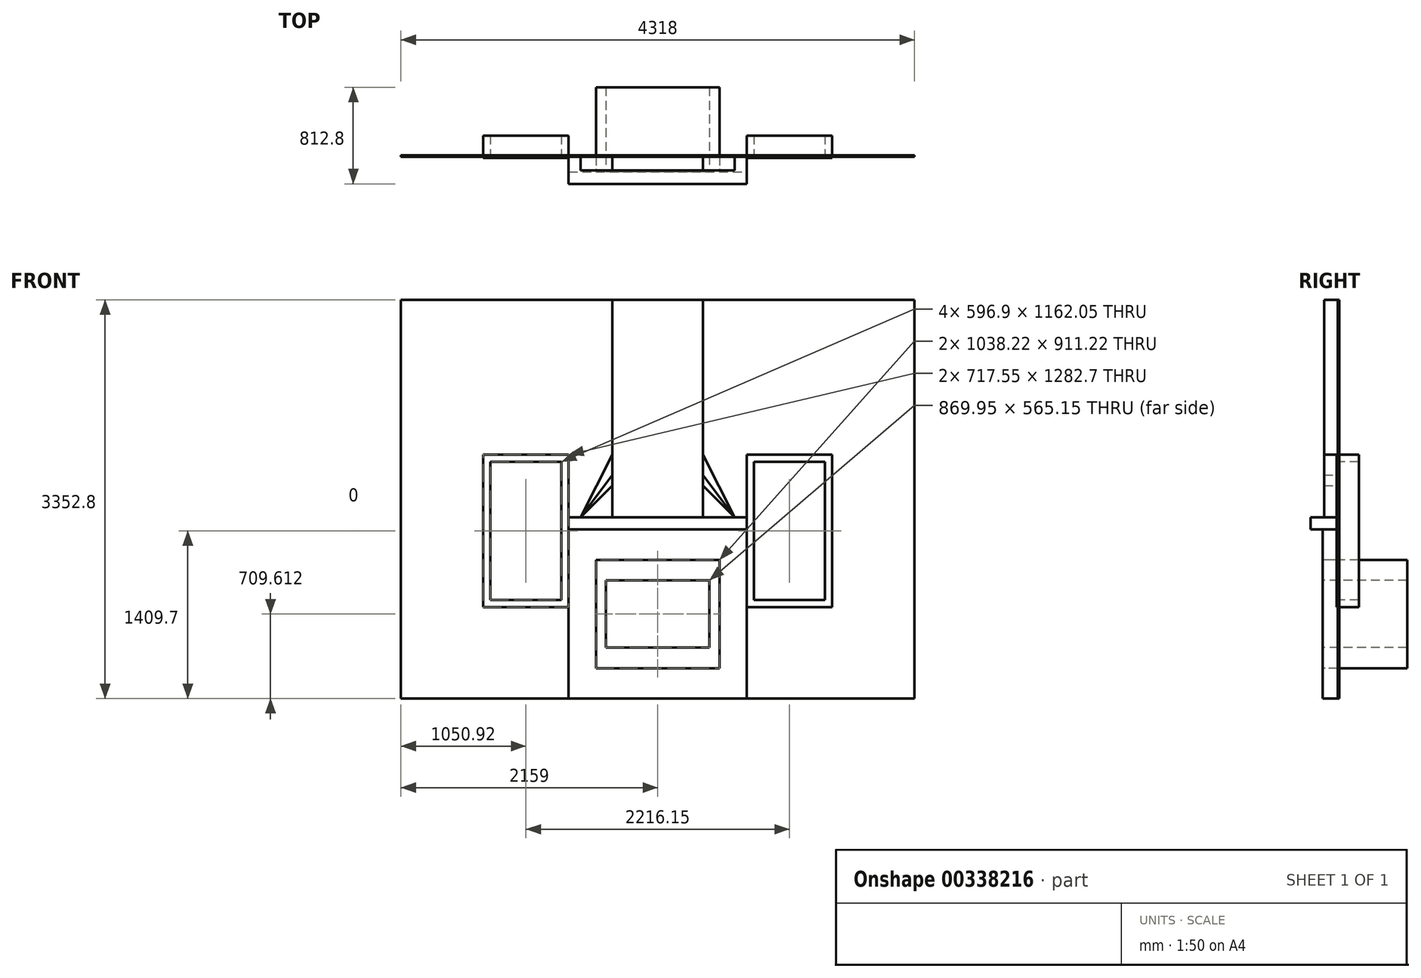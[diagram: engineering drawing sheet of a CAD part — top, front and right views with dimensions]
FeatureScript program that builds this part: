
annotation { "Feature Type Name" : "Feature", "Feature Type Description" : "" }
export const myFeature = defineFeature(function(context is Context, id is Id, definition is map)
    precondition{}
    {
        {
            var Q0;
            Q0=qCreatedBy(makeId("Top.planeOp"),FACE);
            var sketch = newSketch(context, id + "F0", { "sketchPlane" : qUnion([Q0])});
            skLineSegment(sketch, "E0", {"start": v(0, 0) * mm, "end": v(-749.3, 0) * mm, "construction": true});
            skLineSegment(sketch, "E1", {"start": v(-749.3, 0) * mm, "end": v(-749.3, -127) * mm, "construction": true});
            skLineSegment(sketch, "E2", {"start": v(-749.3, -127) * mm, "end": v(749.3, -127) * mm, "construction": true});
            skLineSegment(sketch, "E3", {"start": v(0, 0) * mm, "end": v(-2159, 0) * mm, "construction": true});
            skLineSegment(sketch, "E4", {"start": v(-2159, 0) * mm, "end": v(2159, 0) * mm, "construction": true});
            skLineSegment(sketch, "E5", {"start": v(-2159, 0) * mm, "end": v(-2159, 12.7) * mm, "construction": true});
            skLineSegment(sketch, "E6", {"start": v(-2159, 12.7) * mm, "end": v(-2159, 152.4) * mm, "construction": true});
            skLineSegment(sketch, "E7", {"start": v(-2159, 152.4) * mm, "end": v(-2159, 165.1) * mm, "construction": true});
            skLineSegment(sketch, "E8", {"start": v(-2159, 165.1) * mm, "end": v(-2159, 177.8) * mm, "construction": true});
            skLineSegment(sketch, "E9", {"start": v(-2159, 177.8) * mm, "end": v(2159, 177.8) * mm, "construction": true});
            skLineSegment(sketch, "E10", {"start": v(-2159, 165.1) * mm, "end": v(2159, 165.1) * mm, "construction": true});
            skLineSegment(sketch, "E11", {"start": v(-2159, 152.4) * mm, "end": v(2159, 152.4) * mm, "construction": true});
            skLineSegment(sketch, "E12", {"start": v(-2159, 12.7) * mm, "end": v(2159, 12.7) * mm, "construction": true});
            skSolve(sketch);
        }
        {
            var Q0;
            Q0=qCreatedBy(makeId("Top.planeOp"),FACE);
            var sketch = newSketch(context, id + "F1", { "sketchPlane" : qUnion([Q0])});
            skPoint(sketch, "E13.0", {"position": v(749.3, -127) * mm});
            skPoint(sketch, "E14.0", {"position": v(-749.3, 0) * mm});
            skLineSegment(sketch, "E15.bottom", {"start": v(-749.3, 0) * mm, "end": v(749.3, 0) * mm});
            skLineSegment(sketch, "E15.top", {"start": v(-749.3, -127) * mm, "end": v(749.3, -127) * mm});
            skLineSegment(sketch, "E15.left", {"start": v(-749.3, 0) * mm, "end": v(-749.3, -127) * mm});
            skLineSegment(sketch, "E15.right", {"start": v(749.3, 0) * mm, "end": v(749.3, -127) * mm});
            skSolve(sketch);
        }
        {
            var Q0;
            Q0=makeQuery(id+"F1.imprint","IMPRINT",FACE,{"disambiguationData":[TD([[makeQuery(id+"F1.imprint","IMPRINT",EDGE,{"derivedFrom":sQuery(id+"F1.wireOp",EDGE,"E15.bottom")}),-1.0]])]});
            extrude(context, id + "F2", {"entities" : qUnion([Q0]), "depth" : 1422.4 * mm});
        }
        {
            var Q0;
            Q0=qCreatedBy(makeId("Top.planeOp"),FACE);
            var sketch = newSketch(context, id + "F3", { "sketchPlane" : qUnion([Q0])});
            skPoint(sketch, "E16.0", {"position": v(-2159, 0) * mm});
            skPoint(sketch, "E17.0", {"position": v(2159, 12.7) * mm});
            skLineSegment(sketch, "E18.bottom", {"start": v(2159, 12.7) * mm, "end": v(-2159, 12.7) * mm});
            skLineSegment(sketch, "E18.top", {"start": v(2159, 0) * mm, "end": v(-2159, 0) * mm});
            skLineSegment(sketch, "E18.left", {"start": v(2159, 12.7) * mm, "end": v(2159, 0) * mm});
            skLineSegment(sketch, "E18.right", {"start": v(-2159, 12.7) * mm, "end": v(-2159, 0) * mm});
            skSolve(sketch);
        }
        {
            var Q0;
            Q0=makeQuery(id+"F3.imprint","IMPRINT",FACE,{"disambiguationData":[TD([[makeQuery(id+"F3.imprint","IMPRINT",EDGE,{"derivedFrom":sQuery(id+"F3.wireOp",EDGE,"E18.bottom")}),1.0]])]});
            extrude(context, id + "F4", {"entities" : qUnion([Q0]), "depth" : 3352.8 * mm});
        }
        {
            var Q0;
            Q0=makeQuery(id+"F4.opExtrude","SWEPT_FACE",FACE,{"disambiguationData":[OSD([sQuery(id+"F3.wireOp",EDGE,"E18.top")])]});
            var sketch = newSketch(context, id + "F5", { "sketchPlane" : qUnion([Q0])});
            skPoint(sketch, "E19.0", {"position": v(-749.3, 1422.4) * mm});
            skPoint(sketch, "E20.0", {"position": v(749.3, 1422.4) * mm});
            skLineSegment(sketch, "E21.0", {"start": v(-749.3, 1422.4) * mm, "end": v(749.3, 1422.4) * mm, "construction": true});
            skLineSegment(sketch, "E22", {"start": v(-749.3, 1422.4) * mm, "end": v(-749.3, 1524) * mm, "construction": true});
            skLineSegment(sketch, "E23.bottom", {"start": v(-749.3, 1524) * mm, "end": v(749.3, 1524) * mm});
            skLineSegment(sketch, "E23.top", {"start": v(-749.3, 1422.4) * mm, "end": v(749.3, 1422.4) * mm});
            skLineSegment(sketch, "E23.left", {"start": v(-749.3, 1524) * mm, "end": v(-749.3, 1422.4) * mm});
            skLineSegment(sketch, "E23.right", {"start": v(749.3, 1524) * mm, "end": v(749.3, 1422.4) * mm});
            skSolve(sketch);
        }
        {
            var Q0;
            Q0=makeQuery(id+"F5.imprint","IMPRINT",FACE,{"disambiguationData":[TD([[makeQuery(id+"F5.imprint","IMPRINT",EDGE,{"derivedFrom":sQuery(id+"F5.wireOp",EDGE,"E23.bottom")}),-1.0]])]});
            extrude(context, id + "F6", {"entities" : qUnion([Q0]), "depth" : 228.6 * mm});
        }
        {
            var Q0;
            Q0=makeQuery(id+"F4.opExtrude","SWEPT_FACE",FACE,{"disambiguationData":[OSD([sQuery(id+"F3.wireOp",EDGE,"E18.top")])]});
            var sketch = newSketch(context, id + "F7", { "sketchPlane" : qUnion([Q0])});
            skPoint(sketch, "E24.0", {"position": v(-749.3, 1524) * mm});
            skPoint(sketch, "E25.0", {"position": v(749.3, 1524) * mm});
            skLineSegment(sketch, "E26", {"start": v(-749.3, 1524) * mm, "end": v(-647.7, 1524) * mm, "construction": true});
            skLineSegment(sketch, "E27", {"start": v(749.3, 1524) * mm, "end": v(647.7, 1524) * mm, "construction": true});
            skLineSegment(sketch, "E28", {"start": v(0, 0) * mm, "end": v(0, 3352.8) * mm, "construction": true});
            skPoint(sketch, "E29.0", {"position": v(0, 1524) * mm});
            skLineSegment(sketch, "E30", {"start": v(0, 1524) * mm, "end": v(381, 1524) * mm, "construction": true});
            skLineSegment(sketch, "E31", {"start": v(0, 3352.8) * mm, "end": v(-381, 3352.8) * mm, "construction": true});
            skSolve(sketch);
        }
        {
            var Q0;
            {var subQ0=sQuery(id+"F3.wireOp",EDGE,"E18.top");Q0=makeQuery(id+"F7.imprint","IMPRINT",FACE,{"disambiguationData":[TD([[makeQuery(id+"F7.imprint","IMPRINT",EDGE,{"derivedFrom":makeQuery(id+"F4.opExtrude","CAP_EDGE",EDGE,{"disambiguationData":[OSD([subQ0])],"isStart":true})}),-1.0]])]});}
            var sketch = newSketch(context, id + "F8", { "sketchPlane" : qUnion([Q0])});
            skPoint(sketch, "E32.0", {"position": v(381, 1524) * mm});
            skPoint(sketch, "E33.0", {"position": v(-381, 3352.8) * mm});
            skLineSegment(sketch, "E34.bottom", {"start": v(-381, 3352.8) * mm, "end": v(381, 3352.8) * mm});
            skLineSegment(sketch, "E34.top", {"start": v(-381, 1524) * mm, "end": v(381, 1524) * mm});
            skLineSegment(sketch, "E34.left", {"start": v(-381, 3352.8) * mm, "end": v(-381, 1524) * mm});
            skLineSegment(sketch, "E34.right", {"start": v(381, 3352.8) * mm, "end": v(381, 1524) * mm});
            skSolve(sketch);
        }
        {
            var Q0;
            {var subQ0=sQuery(id+"F3.wireOp",EDGE,"E18.top");Q0=makeQuery(id+"F7.imprint","IMPRINT",FACE,{"disambiguationData":[TD([[makeQuery(id+"F7.imprint","IMPRINT",EDGE,{"derivedFrom":makeQuery(id+"F4.opExtrude","CAP_EDGE",EDGE,{"disambiguationData":[OSD([subQ0])],"isStart":true})}),-1.0]])]});}
            var sketch = newSketch(context, id + "F9", { "sketchPlane" : qUnion([Q0])});
            skPoint(sketch, "E35.0", {"position": v(749.3, 0) * mm});
            skPoint(sketch, "E36.0", {"position": v(-749.3, 0) * mm});
            skLineSegment(sketch, "E37", {"start": v(-749.3, 0) * mm, "end": v(-749.3, 828.68) * mm, "construction": true});
            skLineSegment(sketch, "E38", {"start": v(749.3, 0) * mm, "end": v(749.3, 828.68) * mm, "construction": true});
            skLineSegment(sketch, "E39", {"start": v(749.3, 828.68) * mm, "end": v(809.62, 828.68) * mm, "construction": true});
            skLineSegment(sketch, "E40", {"start": v(-749.3, 828.68) * mm, "end": v(-809.62, 828.68) * mm, "construction": true});
            skLineSegment(sketch, "E41", {"start": v(-809.62, 828.68) * mm, "end": v(-809.62, 1990.73) * mm, "construction": true});
            skLineSegment(sketch, "E42", {"start": v(809.62, 828.68) * mm, "end": v(809.62, 1990.73) * mm, "construction": true});
            skLineSegment(sketch, "E43", {"start": v(809.62, 1990.73) * mm, "end": v(1406.53, 1990.73) * mm, "construction": true});
            skLineSegment(sketch, "E44", {"start": v(-809.62, 1990.73) * mm, "end": v(-1406.53, 1990.73) * mm, "construction": true});
            skLineSegment(sketch, "E45", {"start": v(-1406.53, 1990.73) * mm, "end": v(-1406.53, 2051.05) * mm, "construction": true});
            skLineSegment(sketch, "E46", {"start": v(-1406.53, 2051.05) * mm, "end": v(-1466.85, 2051.05) * mm, "construction": true});
            skLineSegment(sketch, "E47", {"start": v(1406.53, 1990.73) * mm, "end": v(1406.53, 2051.05) * mm, "construction": true});
            skLineSegment(sketch, "E48", {"start": v(1406.53, 2051.05) * mm, "end": v(1466.85, 2051.05) * mm, "construction": true});
            skLineSegment(sketch, "E49", {"start": v(749.3, 828.68) * mm, "end": v(749.3, 768.35) * mm, "construction": true});
            skLineSegment(sketch, "E50", {"start": v(-749.3, 828.68) * mm, "end": v(-749.3, 768.35) * mm, "construction": true});
            skSolve(sketch);
        }
        {
            var Q0;
            {var subQ0=sQuery(id+"F3.wireOp",EDGE,"E18.top");Q0=makeQuery(id+"F7.imprint","IMPRINT",FACE,{"disambiguationData":[TD([[makeQuery(id+"F7.imprint","IMPRINT",EDGE,{"derivedFrom":makeQuery(id+"F4.opExtrude","CAP_EDGE",EDGE,{"disambiguationData":[OSD([subQ0])],"isStart":true})}),-1.0]])]});}
            var sketch = newSketch(context, id + "F10", { "sketchPlane" : qUnion([Q0])});
            skPoint(sketch, "E51.0", {"position": v(-809.62, 828.68) * mm});
            skPoint(sketch, "E52.0", {"position": v(-1406.53, 1990.73) * mm});
            skPoint(sketch, "E53.0", {"position": v(809.62, 828.68) * mm});
            skPoint(sketch, "E54.0", {"position": v(1406.53, 1990.73) * mm});
            skLineSegment(sketch, "E55.bottom", {"start": v(-1406.53, 1990.73) * mm, "end": v(-809.62, 1990.73) * mm});
            skLineSegment(sketch, "E55.top", {"start": v(-1406.53, 828.68) * mm, "end": v(-809.62, 828.68) * mm});
            skLineSegment(sketch, "E55.left", {"start": v(-1406.53, 1990.73) * mm, "end": v(-1406.53, 828.68) * mm});
            skLineSegment(sketch, "E55.right", {"start": v(-809.62, 1990.73) * mm, "end": v(-809.62, 828.68) * mm});
            skLineSegment(sketch, "E56.bottom", {"start": v(1406.53, 1990.73) * mm, "end": v(809.62, 1990.73) * mm});
            skLineSegment(sketch, "E56.top", {"start": v(1406.53, 828.68) * mm, "end": v(809.62, 828.68) * mm});
            skLineSegment(sketch, "E56.left", {"start": v(1406.53, 1990.73) * mm, "end": v(1406.53, 828.68) * mm});
            skLineSegment(sketch, "E56.right", {"start": v(809.62, 1990.73) * mm, "end": v(809.62, 828.68) * mm});
            skSolve(sketch);
        }
        {
            var Q0;
            {var subQ0=sQuery(id+"F3.wireOp",EDGE,"E18.top");Q0=makeQuery(id+"F7.imprint","IMPRINT",FACE,{"disambiguationData":[TD([[makeQuery(id+"F7.imprint","IMPRINT",EDGE,{"derivedFrom":makeQuery(id+"F4.opExtrude","CAP_EDGE",EDGE,{"disambiguationData":[OSD([subQ0])],"isStart":true})}),-1.0]])]});}
            var sketch = newSketch(context, id + "F11", { "sketchPlane" : qUnion([Q0])});
            skPoint(sketch, "E57.0", {"position": v(-1406.53, 1990.73) * mm});
            skPoint(sketch, "E58.0", {"position": v(-1466.85, 2051.05) * mm});
            skPoint(sketch, "E59.0", {"position": v(-809.62, 828.68) * mm});
            skPoint(sketch, "E60.0", {"position": v(-749.3, 768.35) * mm});
            skPoint(sketch, "E61.0", {"position": v(809.62, 828.68) * mm});
            skPoint(sketch, "E62.0", {"position": v(749.3, 768.35) * mm});
            skPoint(sketch, "E63.0", {"position": v(1406.53, 1990.73) * mm});
            skPoint(sketch, "E64.0", {"position": v(1466.85, 2051.05) * mm});
            skLineSegment(sketch, "E65.bottom", {"start": v(-1466.85, 2051.05) * mm, "end": v(-749.3, 2051.05) * mm});
            skLineSegment(sketch, "E65.top", {"start": v(-1466.85, 768.35) * mm, "end": v(-749.3, 768.35) * mm});
            skLineSegment(sketch, "E65.left", {"start": v(-1466.85, 2051.05) * mm, "end": v(-1466.85, 768.35) * mm});
            skLineSegment(sketch, "E65.right", {"start": v(-749.3, 2051.05) * mm, "end": v(-749.3, 768.35) * mm});
            skLineSegment(sketch, "E66.bottom", {"start": v(1466.85, 2051.05) * mm, "end": v(749.3, 2051.05) * mm});
            skLineSegment(sketch, "E66.top", {"start": v(1466.85, 768.35) * mm, "end": v(749.3, 768.35) * mm});
            skLineSegment(sketch, "E66.left", {"start": v(1466.85, 2051.05) * mm, "end": v(1466.85, 768.35) * mm});
            skLineSegment(sketch, "E66.right", {"start": v(749.3, 2051.05) * mm, "end": v(749.3, 768.35) * mm});
            skLineSegment(sketch, "E67.bottom", {"start": v(1406.53, 1990.73) * mm, "end": v(809.62, 1990.73) * mm});
            skLineSegment(sketch, "E67.top", {"start": v(1406.53, 828.68) * mm, "end": v(809.62, 828.68) * mm});
            skLineSegment(sketch, "E67.left", {"start": v(1406.53, 1990.73) * mm, "end": v(1406.53, 828.68) * mm});
            skLineSegment(sketch, "E67.right", {"start": v(809.62, 1990.73) * mm, "end": v(809.62, 828.68) * mm});
            skLineSegment(sketch, "E68.bottom", {"start": v(-1406.53, 1990.73) * mm, "end": v(-809.62, 1990.73) * mm});
            skLineSegment(sketch, "E68.top", {"start": v(-1406.53, 828.68) * mm, "end": v(-809.62, 828.68) * mm});
            skLineSegment(sketch, "E68.left", {"start": v(-1406.53, 1990.73) * mm, "end": v(-1406.53, 828.68) * mm});
            skLineSegment(sketch, "E68.right", {"start": v(-809.62, 1990.73) * mm, "end": v(-809.62, 828.68) * mm});
            skSolve(sketch);
        }
        {
            var Q0;
            Q0=makeQuery(id+"F11.imprint","IMPRINT",FACE,{"disambiguationData":[TD([[makeQuery(id+"F11.imprint","IMPRINT",EDGE,{"derivedFrom":sQuery(id+"F11.wireOp",EDGE,"E65.bottom")}),-1.0]])]});
            var Q1;
            Q1=makeQuery(id+"F11.imprint","IMPRINT",FACE,{"disambiguationData":[TD([[makeQuery(id+"F11.imprint","IMPRINT",EDGE,{"derivedFrom":sQuery(id+"F11.wireOp",EDGE,"E66.bottom")}),1.0]])]});
            extrude(context, id + "F12", {"entities" : qUnion([Q0, Q1]), "operationType" : NewBodyOperationType.REMOVE, "oppositeDirection" : true, "depth" : 25.4 * mm});
        }
        {
            var Q0;
            Q0=makeQuery(id+"F8.imprint","IMPRINT",FACE,{"disambiguationData":[TD([[makeQuery(id+"F8.imprint","IMPRINT",EDGE,{"derivedFrom":sQuery(id+"F8.wireOp",EDGE,"E34.top")}),-1.0]])]});
            var sketch = newSketch(context, id + "F13", { "sketchPlane" : qUnion([Q0])});
            skPoint(sketch, "E69.0", {"position": v(-749.3, 2051.05) * mm});
            skPoint(sketch, "E70.0", {"position": v(749.3, 2051.05) * mm});
            skPoint(sketch, "E71.0", {"position": v(381, 1524) * mm});
            skPoint(sketch, "E72.0", {"position": v(-381, 1524) * mm});
            skPoint(sketch, "E73.0", {"position": v(-647.7, 1524) * mm});
            skPoint(sketch, "E74.0", {"position": v(647.7, 1524) * mm});
            skPoint(sketch, "E75.0", {"position": v(381, 3352.8) * mm});
            skPoint(sketch, "E76.0", {"position": v(-381, 3352.8) * mm});
            skLineSegment(sketch, "E77", {"start": v(-749.3, 2051.05) * mm, "end": v(749.3, 2051.05) * mm, "construction": true});
            skLineSegment(sketch, "E78", {"start": v(-381, 1524) * mm, "end": v(-381, 2051.05) * mm, "construction": true});
            skLineSegment(sketch, "E79", {"start": v(381, 1524) * mm, "end": v(381, 2051.05) * mm, "construction": true});
            skLineSegment(sketch, "E80", {"start": v(-647.7, 1524) * mm, "end": v(-381, 1524) * mm, "construction": true});
            skLineSegment(sketch, "E81", {"start": v(381, 1524) * mm, "end": v(647.7, 1524) * mm, "construction": true});
            skLineSegment(sketch, "E82", {"start": v(381, 1524) * mm, "end": v(381, 1790.7) * mm, "construction": true});
            skLineSegment(sketch, "E83", {"start": v(-381, 1524) * mm, "end": v(-381, 1790.7) * mm, "construction": true});
            skLineSegment(sketch, "E84", {"start": v(-381, 1524) * mm, "end": v(-381, 1879.6) * mm, "construction": true});
            skLineSegment(sketch, "E85", {"start": v(381, 1524) * mm, "end": v(381, 1879.6) * mm, "construction": true});
            skSolve(sketch);
        }
        {
            var Q0;
            Q0=makeQuery(id+"F11.imprint","IMPRINT",FACE,{"disambiguationData":[TD([[makeQuery(id+"F11.imprint","IMPRINT",EDGE,{"derivedFrom":sQuery(id+"F11.wireOp",EDGE,"E65.bottom")}),1.0]])]});
            var sketch = newSketch(context, id + "F14", { "sketchPlane" : qUnion([Q0])});
            skPoint(sketch, "E86.0", {"position": v(-647.7, 1524) * mm});
            skPoint(sketch, "E87.0", {"position": v(647.7, 1524) * mm});
            skPoint(sketch, "E88.0", {"position": v(381, 1790.7) * mm});
            skPoint(sketch, "E89.0", {"position": v(-381, 1790.7) * mm});
            skPoint(sketch, "E90.0", {"position": v(-381, 3352.8) * mm});
            skPoint(sketch, "E91.0", {"position": v(381, 3352.8) * mm});
            skLineSegment(sketch, "E92", {"start": v(-647.7, 1524) * mm, "end": v(647.7, 1524) * mm});
            skLineSegment(sketch, "E93", {"start": v(647.7, 1524) * mm, "end": v(381, 1790.7) * mm});
            skLineSegment(sketch, "E94", {"start": v(381, 1790.7) * mm, "end": v(381, 3352.8) * mm});
            skLineSegment(sketch, "E95", {"start": v(381, 3352.8) * mm, "end": v(-381, 3352.8) * mm});
            skLineSegment(sketch, "E96", {"start": v(-381, 3352.8) * mm, "end": v(-381, 1790.7) * mm});
            skLineSegment(sketch, "E97", {"start": v(-381, 1790.7) * mm, "end": v(-647.7, 1524) * mm});
            skSolve(sketch);
        }
        {
            var Q0;
            Q0=makeQuery(id+"F11.imprint","IMPRINT",FACE,{"disambiguationData":[TD([[makeQuery(id+"F11.imprint","IMPRINT",EDGE,{"derivedFrom":sQuery(id+"F11.wireOp",EDGE,"E65.bottom")}),1.0]])]});
            var sketch = newSketch(context, id + "F15", { "sketchPlane" : qUnion([Q0])});
            skPoint(sketch, "E98.0", {"position": v(-647.7, 1524) * mm});
            skPoint(sketch, "E99.0", {"position": v(647.7, 1524) * mm});
            skPoint(sketch, "E100.0", {"position": v(381, 1879.6) * mm});
            skPoint(sketch, "E101.0", {"position": v(-381, 1879.6) * mm});
            skPoint(sketch, "E102.0", {"position": v(-381, 3352.8) * mm});
            skPoint(sketch, "E103.0", {"position": v(381, 3352.8) * mm});
            skLineSegment(sketch, "E104", {"start": v(-647.7, 1524) * mm, "end": v(647.7, 1524) * mm});
            skLineSegment(sketch, "E105", {"start": v(647.7, 1524) * mm, "end": v(381, 1879.6) * mm});
            skLineSegment(sketch, "E106", {"start": v(381, 1879.6) * mm, "end": v(381, 3352.8) * mm});
            skLineSegment(sketch, "E107", {"start": v(381, 3352.8) * mm, "end": v(-381, 3352.8) * mm});
            skLineSegment(sketch, "E108", {"start": v(-381, 3352.8) * mm, "end": v(-381, 1879.6) * mm});
            skLineSegment(sketch, "E109", {"start": v(-381, 1879.6) * mm, "end": v(-647.7, 1524) * mm});
            skSolve(sketch);
        }
        {
            var Q0;
            Q0=makeQuery(id+"F11.imprint","IMPRINT",FACE,{"disambiguationData":[TD([[makeQuery(id+"F11.imprint","IMPRINT",EDGE,{"derivedFrom":sQuery(id+"F11.wireOp",EDGE,"E65.bottom")}),1.0]])]});
            var sketch = newSketch(context, id + "F16", { "sketchPlane" : qUnion([Q0])});
            skPoint(sketch, "E110.0", {"position": v(-381, 3352.8) * mm});
            skPoint(sketch, "E111.0", {"position": v(-381, 2051.05) * mm});
            skPoint(sketch, "E112.0", {"position": v(-647.7, 1524) * mm});
            skPoint(sketch, "E113.0", {"position": v(647.7, 1524) * mm});
            skPoint(sketch, "E114.0", {"position": v(381, 2051.05) * mm});
            skPoint(sketch, "E115.0", {"position": v(381, 3352.8) * mm});
            skLineSegment(sketch, "E116", {"start": v(-381, 3352.8) * mm, "end": v(-381, 2051.05) * mm});
            skLineSegment(sketch, "E117", {"start": v(-381, 2051.05) * mm, "end": v(-647.7, 1524) * mm});
            skLineSegment(sketch, "E118", {"start": v(-647.7, 1524) * mm, "end": v(647.7, 1524) * mm});
            skLineSegment(sketch, "E119", {"start": v(647.7, 1524) * mm, "end": v(381, 2051.05) * mm});
            skLineSegment(sketch, "E120", {"start": v(381, 2051.05) * mm, "end": v(381, 3352.8) * mm});
            skLineSegment(sketch, "E121", {"start": v(381, 3352.8) * mm, "end": v(-381, 3352.8) * mm});
            skSolve(sketch);
        }
        {
            var Q0;
            Q0=makeQuery(id+"F8.imprint","IMPRINT",FACE,{"disambiguationData":[TD([[makeQuery(id+"F8.imprint","IMPRINT",EDGE,{"derivedFrom":sQuery(id+"F8.wireOp",EDGE,"E34.bottom")}),1.0]])]});
            extrude(context, id + "F17", {"entities" : qUnion([Q0]), "depth" : 114.3 * mm});
        }
        {
            var Q0;
            Q0 = qSketchRegion(id + "F14", true);
            extrude(context, id + "F18", {"entities" : qUnion([Q0]), "depth" : 114.3 * mm});
        }
        {
            var Q0;
            Q0 = qSketchRegion(id + "F15", true);
            extrude(context, id + "F19", {"entities" : qUnion([Q0]), "depth" : 114.3 * mm});
        }
        {
            var Q0;
            Q0 = qSketchRegion(id + "F16", true);
            extrude(context, id + "F20", {"entities" : qUnion([Q0]), "depth" : 114.3 * mm});
        }
        {
            var Q0;
            Q0=makeQuery(id+"F11.imprint","IMPRINT",FACE,{"disambiguationData":[TD([[makeQuery(id+"F11.imprint","IMPRINT",EDGE,{"derivedFrom":sQuery(id+"F11.wireOp",EDGE,"E65.bottom")}),-1.0]])]});
            var Q1;
            Q1=makeQuery(id+"F11.imprint","IMPRINT",FACE,{"disambiguationData":[TD([[makeQuery(id+"F11.imprint","IMPRINT",EDGE,{"derivedFrom":sQuery(id+"F11.wireOp",EDGE,"E66.bottom")}),1.0]])]});
            extrude(context, id + "F21", {"entities" : qUnion([Q0, Q1]), "oppositeDirection" : true, "depth" : 177.8 * mm});
        }
        {
            var Q0;
            Q0=makeQuery(id+"F11.imprint","IMPRINT",FACE,{"disambiguationData":[TD([[makeQuery(id+"F11.imprint","IMPRINT",EDGE,{"derivedFrom":sQuery(id+"F11.wireOp",EDGE,"E65.bottom")}),-1.0]])]});
            var Q1;
            Q1=makeQuery(id+"F11.imprint","IMPRINT",FACE,{"disambiguationData":[TD([[makeQuery(id+"F11.imprint","IMPRINT",EDGE,{"derivedFrom":sQuery(id+"F11.wireOp",EDGE,"E66.bottom")}),1.0]])]});
            extrude(context, id + "F22", {"entities" : qUnion([Q0, Q1]), "depth" : 9.52 * mm});
        }
        {
            var Q0;
            Q0=makeQuery(id+"F2.opExtrude","SWEPT_FACE",FACE,{"disambiguationData":[OSD([sQuery(id+"F1.wireOp",EDGE,"E15.top")])]});
            var sketch = newSketch(context, id + "F23", { "sketchPlane" : qUnion([Q0])});
            skPoint(sketch, "E122.0", {"position": v(0, 0) * mm});
            skLineSegment(sketch, "E123", {"start": v(0, 0) * mm, "end": v(-519.11, 0) * mm, "construction": true});
            skLineSegment(sketch, "E124", {"start": v(-519.11, 0) * mm, "end": v(-519.11, 254) * mm, "construction": true});
            skLineSegment(sketch, "E125", {"start": v(-519.11, 254) * mm, "end": v(519.11, 254) * mm, "construction": true});
            skLineSegment(sketch, "E126", {"start": v(519.11, 254) * mm, "end": v(519.11, 1165.23) * mm, "construction": true});
            skLineSegment(sketch, "E127", {"start": v(0, 0) * mm, "end": v(0, 254) * mm, "construction": true});
            skLineSegment(sketch, "E128", {"start": v(0, 254) * mm, "end": v(0, 427.04) * mm, "construction": true});
            skLineSegment(sketch, "E129", {"start": v(0, 427.04) * mm, "end": v(-434.98, 427.04) * mm, "construction": true});
            skLineSegment(sketch, "E130", {"start": v(-434.98, 427.04) * mm, "end": v(-434.98, 992.19) * mm, "construction": true});
            skLineSegment(sketch, "E131.bottom", {"start": v(-519.11, 254) * mm, "end": v(519.11, 254) * mm});
            skLineSegment(sketch, "E131.top", {"start": v(-519.11, 1165.23) * mm, "end": v(519.11, 1165.23) * mm});
            skLineSegment(sketch, "E131.left", {"start": v(-519.11, 254) * mm, "end": v(-519.11, 1165.23) * mm});
            skLineSegment(sketch, "E131.right", {"start": v(519.11, 254) * mm, "end": v(519.11, 1165.23) * mm});
            skLineSegment(sketch, "E132", {"start": v(-434.98, 992.19) * mm, "end": v(434.97, 992.19) * mm, "construction": true});
            skLineSegment(sketch, "E133.bottom", {"start": v(434.97, 992.19) * mm, "end": v(-434.98, 992.19) * mm});
            skLineSegment(sketch, "E133.top", {"start": v(434.97, 427.04) * mm, "end": v(-434.98, 427.04) * mm});
            skLineSegment(sketch, "E133.left", {"start": v(434.97, 992.19) * mm, "end": v(434.97, 427.04) * mm});
            skLineSegment(sketch, "E133.right", {"start": v(-434.98, 992.19) * mm, "end": v(-434.98, 427.04) * mm});
            skSolve(sketch);
        }
        {
            var Q0;
            Q0=makeQuery(id+"F23.imprint","IMPRINT",FACE,{"disambiguationData":[TD([[makeQuery(id+"F23.imprint","IMPRINT",EDGE,{"derivedFrom":sQuery(id+"F23.wireOp",EDGE,"E131.bottom")}),1.0]])]});
            var Q1;
            Q1=makeQuery(id+"F23.imprint","IMPRINT",FACE,{"disambiguationData":[TD([[makeQuery(id+"F23.imprint","IMPRINT",EDGE,{"derivedFrom":sQuery(id+"F23.wireOp",EDGE,"E133.bottom")}),1.0]])]});
            extrude(context, id + "F24", {"entities" : qUnion([Q0, Q1]), "operationType" : NewBodyOperationType.REMOVE, "oppositeDirection" : true, "depth" : 711.2 * mm});
        }
        {
            var Q0;
            Q0=makeQuery(id+"F23.imprint","IMPRINT",FACE,{"disambiguationData":[TD([[makeQuery(id+"F23.imprint","IMPRINT",EDGE,{"derivedFrom":sQuery(id+"F23.wireOp",EDGE,"E131.bottom")}),1.0]])]});
            extrude(context, id + "F25", {"entities" : qUnion([Q0]), "oppositeDirection" : true, "depth" : 711.2 * mm});
        }
    });
